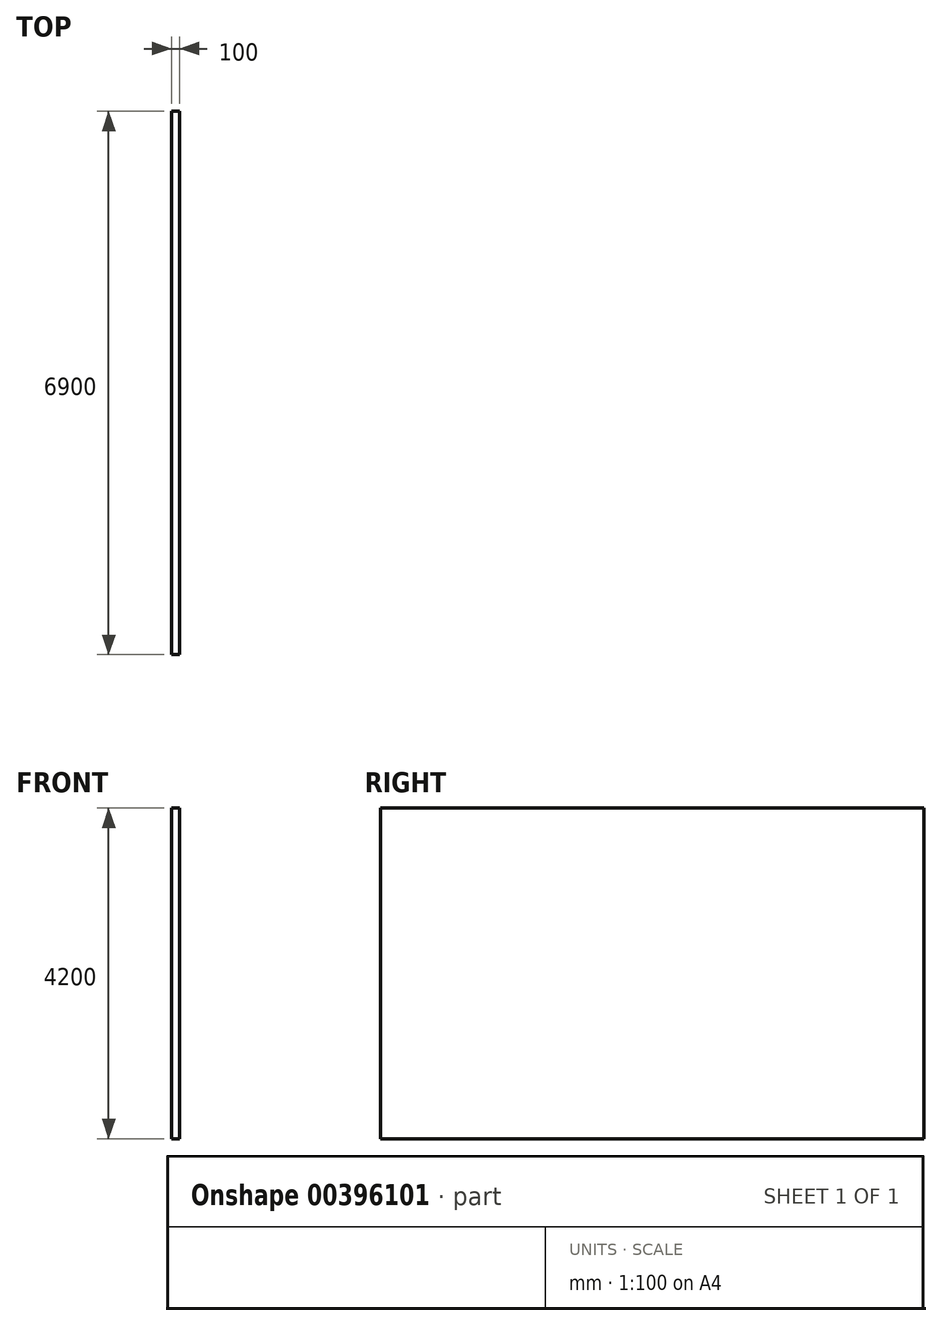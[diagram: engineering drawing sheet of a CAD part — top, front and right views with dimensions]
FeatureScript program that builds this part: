
annotation { "Feature Type Name" : "Feature", "Feature Type Description" : "" }
export const myFeature = defineFeature(function(context is Context, id is Id, definition is map)
    precondition{}
    {
        {
            var Q0;
            Q0=qCreatedBy(makeId("Top.planeOp"),FACE);
            var sketch = newSketch(context, id + "F0", { "sketchPlane" : qUnion([Q0])});
            skLineSegment(sketch, "E0.bottom", {"start": v(0, 0) * mm, "end": v(100, 0) * mm});
            skLineSegment(sketch, "E0.top", {"start": v(0, 6900) * mm, "end": v(100, 6900) * mm});
            skLineSegment(sketch, "E0.left", {"start": v(0, 0) * mm, "end": v(0, 6900) * mm});
            skLineSegment(sketch, "E0.right", {"start": v(100, 0) * mm, "end": v(100, 6900) * mm});
            skSolve(sketch);
        }
        {
            var Q0;
            Q0=makeQuery(id+"F0.imprint","IMPRINT",FACE,{"disambiguationData":[TD([[makeQuery(id+"F0.imprint","IMPRINT",EDGE,{"derivedFrom":sQuery(id+"F0.wireOp",EDGE,"E0.bottom")}),1.0]])]});
            extrude(context, id + "F1", {"entities" : qUnion([Q0]), "depth" : 4200 * mm});
        }
    });
